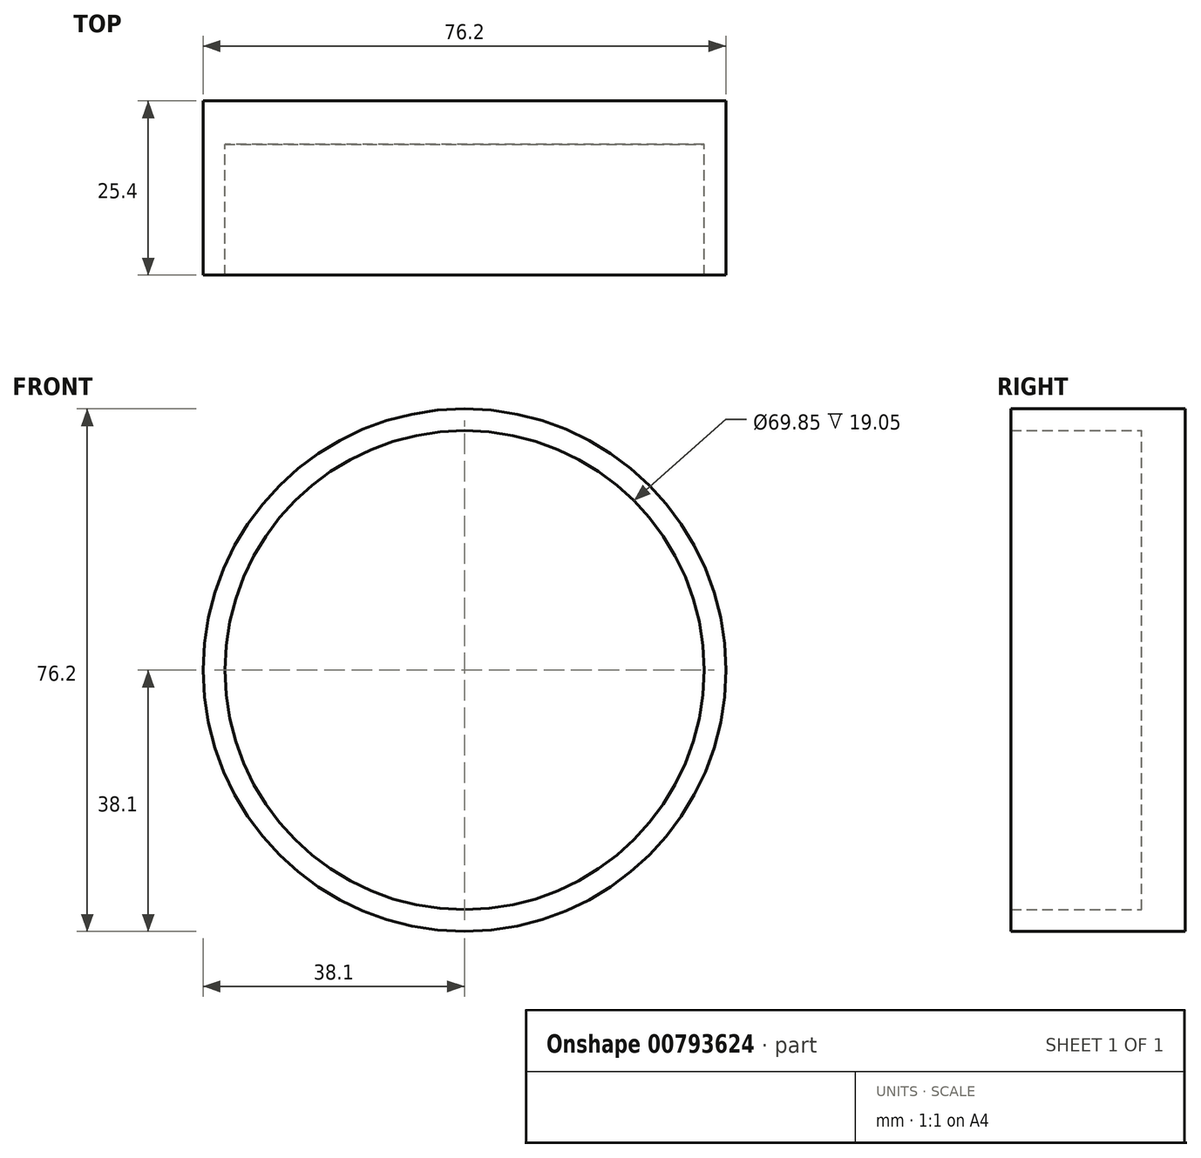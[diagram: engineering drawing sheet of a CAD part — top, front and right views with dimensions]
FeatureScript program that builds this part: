
annotation { "Feature Type Name" : "Feature", "Feature Type Description" : "" }
export const myFeature = defineFeature(function(context is Context, id is Id, definition is map)
    precondition{}
    {
        {
            var Q0;
            Q0=qCreatedBy(makeId("Front.planeOp"),FACE);
            var sketch = newSketch(context, id + "F0", { "sketchPlane" : qUnion([Q0])});
            skCircle(sketch, "E0", {"center": v(0, 0) * mm, "radius": 38.1 * mm});
            skSolve(sketch);
        }
        {
            var Q0;
            Q0 = qSketchRegion(id + "F0", true);
            extrude(context, id + "F1", {"entities" : qUnion([Q0]), "oppositeDirection" : true, "depth" : 6.35 * mm, "offsetDistance" : 25.4 * mm});
        }
        {
            var Q0;
            Q0=makeQuery(id+"F1.opExtrude","CAP_FACE",FACE,{"disambiguationData":[OSD([sQuery(id+"F0.wireOp",EDGE,"E0")])],"isStart":true});
            var sketch = newSketch(context, id + "F2", { "sketchPlane" : qUnion([Q0])});
            skCircle(sketch, "E1", {"center": v(0, 0) * mm, "radius": 34.93 * mm});
            skSolve(sketch);
        }
        {
            var Q0;
            Q0=makeQuery(id+"F2.imprint","IMPRINT",FACE,{"disambiguationData":[TD([[makeQuery(id+"F2.imprint","IMPRINT",EDGE,{"derivedFrom":sQuery(id+"F2.wireOp",EDGE,"E1")}),-1.0]])]});
            var sketch = newSketch(context, id + "F3", { "sketchPlane" : qUnion([Q0])});
            skSolve(sketch);
        }
        {
            var Q0;
            Q0 = qSketchRegion(id + "F3", true);
            var Q1;
            Q1=makeQuery(id+"F2.imprint","IMPRINT",FACE,{"disambiguationData":[TD([[makeQuery(id+"F2.imprint","IMPRINT",EDGE,{"derivedFrom":sQuery(id+"F2.wireOp",EDGE,"E1")}),-1.0]])]});
            extrude(context, id + "F4", {"entities" : qUnion([Q0, Q1]), "operationType" : NewBodyOperationType.ADD, "depth" : 19.05 * mm, "offsetDistance" : 25.4 * mm});
        }
        {
            var Q0;
            Q0=qCreatedBy(makeId("Front.planeOp"),FACE);
            cPlane(context, id + "F5", {"entities" : qUnion([Q0]), "cplaneType" : CPlaneType.OFFSET, "offset" : 19.05 * mm, "width" : 152.4 * mm, "height" : 152.4 * mm});
        }
    });
